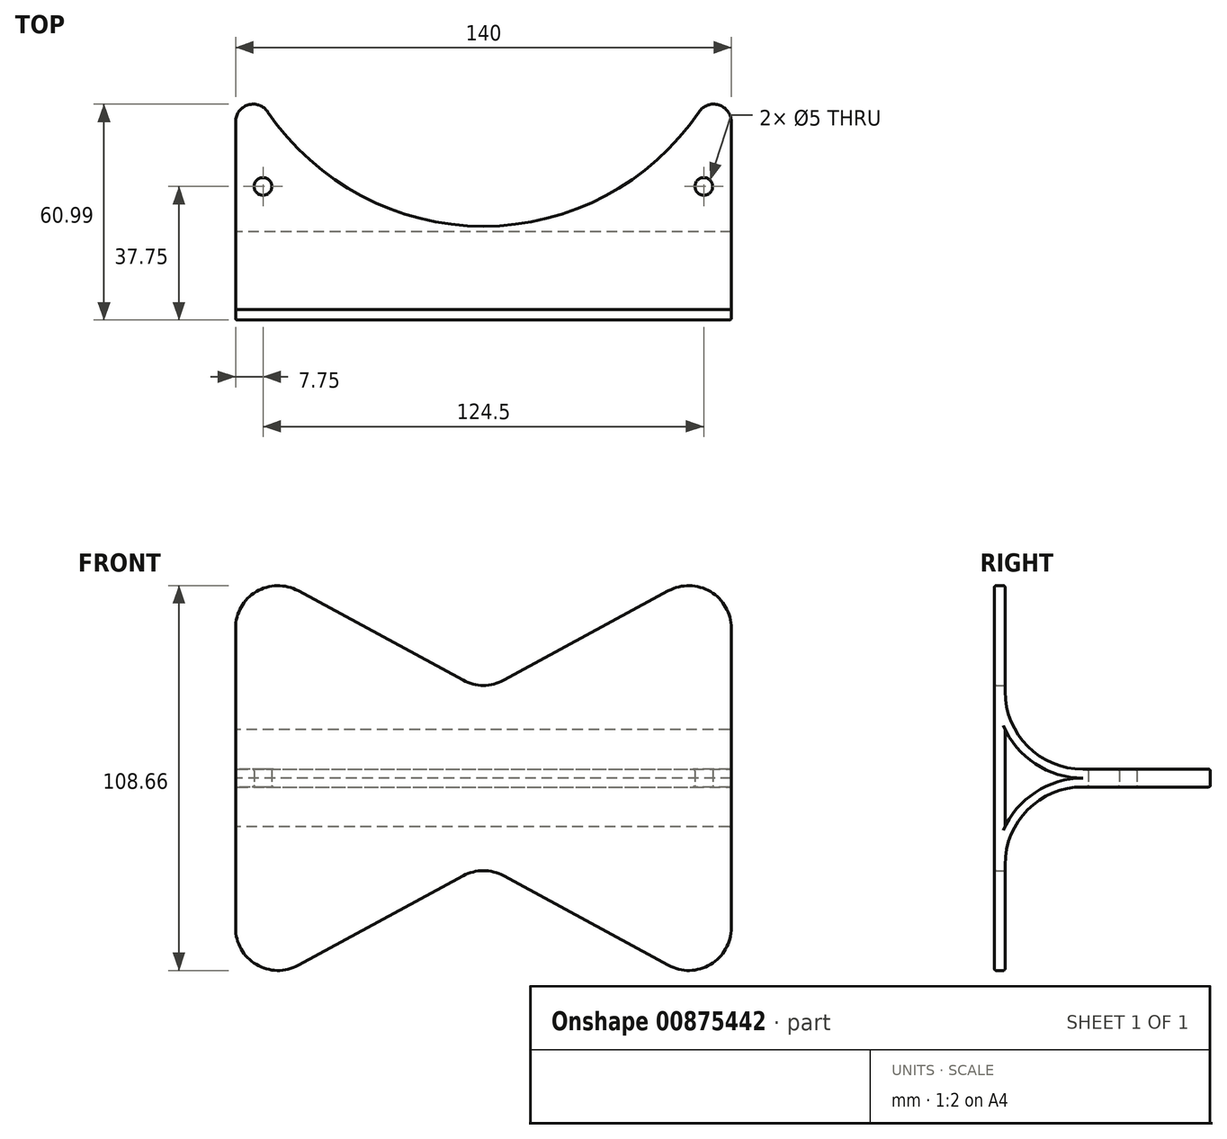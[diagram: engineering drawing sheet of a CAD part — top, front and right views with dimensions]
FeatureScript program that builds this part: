
annotation { "Feature Type Name" : "Feature", "Feature Type Description" : "" }
export const myFeature = defineFeature(function(context is Context, id is Id, definition is map)
    precondition{}
    {
        {
            var Q0;
            Q0=qCreatedBy(makeId("Top.planeOp"),FACE);
            var sketch = newSketch(context, id + "F0", { "sketchPlane" : qUnion([Q0])});
            skArc(sketch, "E0", {"start": v(-70, -22.41) * mm, "mid": v(0, -73.5) * mm, "end": v(70, -22.41) * mm});
            skLineSegment(sketch, "E1", {"start": v(-70, -22.41) * mm, "end": v(-70, -75) * mm});
            skLineSegment(sketch, "E2", {"start": v(-70, -75) * mm, "end": v(70, -75) * mm});
            skLineSegment(sketch, "E3", {"start": v(70, -75) * mm, "end": v(70, -22.41) * mm});
            skCircle(sketch, "E4", {"center": v(62.25, -62.25) * mm, "radius": 2.5 * mm});
            skLineSegment(sketch, "E5", {"start": v(0, 26.99) * mm, "end": v(0, -105.78) * mm, "construction": true});
            skCircle(sketch, "E6.MirrorC", {"center": v(-62.25, -62.25) * mm, "radius": 2.5 * mm});
            skSolve(sketch);
        }
        {
            var Q0;
            Q0=qSketchRegion(id+"F0",true);
            extrude(context, id + "F1", {"entities" : qUnion([Q0]), "depth" : 5 * mm, "offsetDistance" : 25 * mm});
        }
        {
            var Q0;
            Q0=makeQuery(id+"F1.opExtrude","SWEPT_FACE",FACE,{"disambiguationData":[OSD([sQuery(id+"F0.wireOp",EDGE,"E1")])]});
            var sketch = newSketch(context, id + "F2", { "sketchPlane" : qUnion([Q0])});
            skArc(sketch, "E7", {"start": v(97, -22) * mm, "mid": v(90.56, -6.44) * mm, "end": v(75, 0) * mm});
            skArc(sketch, "E8", {"start": v(75, 5) * mm, "mid": v(90.56, 11.44) * mm, "end": v(97, 27) * mm});
            skLineSegment(sketch, "E9.bottom", {"start": v(97, -60) * mm, "end": v(100, -60) * mm});
            skLineSegment(sketch, "E9.top", {"start": v(97, 65) * mm, "end": v(100, 65) * mm});
            skLineSegment(sketch, "E9.left", {"start": v(97, -60) * mm, "end": v(97, -22) * mm});
            skLineSegment(sketch, "E9.right", {"start": v(100, -60) * mm, "end": v(100, 65) * mm});
            skArc(sketch, "E10", {"start": v(97, -11.22) * mm, "mid": v(87.96, -1.21) * mm, "end": v(75, 2.5) * mm});
            skArc(sketch, "E11", {"start": v(75, 2.5) * mm, "mid": v(87.96, 6.21) * mm, "end": v(97, 16.22) * mm});
            skLineSegment(sketch, "E12", {"start": v(75, 0) * mm, "end": v(75, 2.5) * mm});
            skLineSegment(sketch, "E13", {"start": v(75, 2.5) * mm, "end": v(75, 5) * mm});
            skLineSegment(sketch, "E14.trimOffspring", {"start": v(97, -11.22) * mm, "end": v(97, 16.22) * mm});
            skLineSegment(sketch, "E15.trimOffspring", {"start": v(97, 27) * mm, "end": v(97, 65) * mm});
            skSolve(sketch);
        }
        {
            var Q0;
            Q0=qSketchRegion(id+"F2",true);
            var Q1;
            Q1=makeQuery(id+"F1.opExtrude","SWEPT_FACE",FACE,{"disambiguationData":[OSD([sQuery(id+"F0.wireOp",EDGE,"E3")])]});
            extrude(context, id + "F3", {"entities" : qUnion([Q0]), "operationType" : NewBodyOperationType.ADD, "endBound" : BoundingType.UP_TO_SURFACE, "oppositeDirection" : true, "depth" : 25 * mm, "endBoundEntityFace" : qUnion([Q1]), "offsetDistance" : 25 * mm});
        }
        {
            var Q0;
            Q0=makeQuery(id+"F2.imprint","IMPRINT",FACE,{"disambiguationData":[TD([[makeQuery(id+"F2.imprint","IMPRINT",EDGE,{"derivedFrom":sQuery(id+"F2.wireOp",EDGE,"E10")}),-1.0]])]});
            extrude(context, id + "F4", {"entities" : qUnion([Q0]), "operationType" : NewBodyOperationType.REMOVE, "endBound" : BoundingType.THROUGH_ALL, "oppositeDirection" : true, "depth" : 25 * mm, "offsetDistance" : 25 * mm});
        }
        {
            var Q0;
            Q0=makeQuery(id+"F1.opExtrude","SWEPT_EDGE",EDGE,{"disambiguationData":[OSD([sQuery(id+"F0.wireOp",EDGE,"E0"),sQuery(id+"F0.wireOp",EDGE,"E3")])]});
            var Q1;
            Q1=makeQuery(id+"F1.opExtrude","SWEPT_EDGE",EDGE,{"disambiguationData":[OSD([sQuery(id+"F0.wireOp",EDGE,"E0"),sQuery(id+"F0.wireOp",EDGE,"E1")])]});
            fillet(context, id + "F5", {"entities" : qUnion([Q0, Q1]), "radius" : 5 * mm, "tangentPropagation" : true, "allowEdgeOverflow" : false});
        }
        {
            var Q0;
            Q0=makeQuery(id+"F3.opExtrude","SWEPT_FACE",FACE,{"disambiguationData":[OSD([sQuery(id+"F2.wireOp",EDGE,"E15.trimOffspring")])]});
            var sketch = newSketch(context, id + "F6", { "sketchPlane" : qUnion([Q0])});
            skPoint(sketch, "E16.middle", {"position": v(0, 46) * mm});
            skLineSegment(sketch, "E17", {"start": v(-105.3, 2.5) * mm, "end": v(109.3, 2.5) * mm, "construction": true});
            skLineSegment(sketch, "E18", {"start": v(0, 17.77) * mm, "end": v(0, 82.4) * mm, "construction": true});
            skPoint(sketch, "E18.startSnap0", {"position": v(0, 27) * mm});
            skLineSegment(sketch, "E19.MirrorCS", {"start": v(70, 65) * mm, "end": v(0, 27) * mm});
            skLineSegment(sketch, "E20", {"start": v(70, 65) * mm, "end": v(0, 65) * mm});
            skLineSegment(sketch, "E21.MirrorCS", {"start": v(-70, 65) * mm, "end": v(0, 65) * mm});
            skLineSegment(sketch, "E22.MirrorCS", {"start": v(-70, 65) * mm, "end": v(0, 27) * mm});
            skLineSegment(sketch, "E23.MirrorCS", {"start": v(70, -60) * mm, "end": v(0, -22) * mm});
            skLineSegment(sketch, "E24.MirrorCS", {"start": v(-70, -60) * mm, "end": v(0, -22) * mm});
            skLineSegment(sketch, "E25.MirrorCS", {"start": v(-70, -60) * mm, "end": v(0, -60) * mm});
            skLineSegment(sketch, "E26.MirrorCS", {"start": v(70, -60) * mm, "end": v(0, -60) * mm});
            skSolve(sketch);
        }
        {
            var Q0;
            Q0=qSketchRegion(id+"F6",true);
            extrude(context, id + "F7", {"entities" : qUnion([Q0]), "operationType" : NewBodyOperationType.REMOVE, "endBound" : BoundingType.THROUGH_ALL, "oppositeDirection" : true, "depth" : 25 * mm, "offsetDistance" : 25 * mm});
        }
        {
            var Q0;
            Q0=makeQuery(id+"F7.boolean.opBoolean","COPY",EDGE,{"derivedFrom":makeQuery(id+"F7.opExtrude","SWEPT_EDGE",EDGE,{"disambiguationData":[OSD([sQuery(id+"F2.wireOp",EDGE,"E8"),sQuery(id+"F2.wireOp",EDGE,"E15.trimOffspring"),sQuery(id+"F6.wireOp",EDGE,"E19.MirrorCS"),sQuery(id+"F6.wireOp",EDGE,"E22.MirrorCS")])]})});
            var Q1;
            Q1=makeQuery(id+"F7.boolean.opBoolean","MERGE",EDGE,{"derivedFrom":[makeQuery(id+"F3.opExtrude","CAP_EDGE",EDGE,{"disambiguationData":[OSD([sQuery(id+"F2.wireOp",EDGE,"E9.top")])],"isStart":true})],"fromTools":[makeQuery(id+"F7.opExtrude","SWEPT_EDGE",EDGE,{"disambiguationData":[OSD([sQuery(id+"F2.wireOp",EDGE,"E15.trimOffspring"),sQuery(id+"F6.wireOp",EDGE,"E19.MirrorCS"),sQuery(id+"F6.wireOp",EDGE,"E20")])]})]});
            var Q2;
            Q2=makeQuery(id+"F7.boolean.opBoolean","MERGE",EDGE,{"derivedFrom":[makeQuery(id+"F3.opExtrude","CAP_EDGE",EDGE,{"disambiguationData":[OSD([sQuery(id+"F2.wireOp",EDGE,"E9.top")])],"isStart":false})],"fromTools":[makeQuery(id+"F7.opExtrude","SWEPT_EDGE",EDGE,{"disambiguationData":[OSD([sQuery(id+"F2.wireOp",EDGE,"E15.trimOffspring"),sQuery(id+"F6.wireOp",EDGE,"E21.MirrorCS"),sQuery(id+"F6.wireOp",EDGE,"E22.MirrorCS")])]})]});
            var Q3;
            Q3=makeQuery(id+"F7.boolean.opBoolean","COPY",EDGE,{"derivedFrom":makeQuery(id+"F7.opExtrude","SWEPT_EDGE",EDGE,{"disambiguationData":[OSD([sQuery(id+"F6.wireOp",EDGE,"E23.MirrorCS"),sQuery(id+"F6.wireOp",EDGE,"E24.MirrorCS")])]})});
            var Q4;
            Q4=makeQuery(id+"F7.boolean.opBoolean","MERGE",EDGE,{"derivedFrom":[makeQuery(id+"F3.opExtrude","CAP_EDGE",EDGE,{"disambiguationData":[OSD([sQuery(id+"F2.wireOp",EDGE,"E9.bottom")])],"isStart":true})],"fromTools":[makeQuery(id+"F7.opExtrude","SWEPT_EDGE",EDGE,{"disambiguationData":[OSD([sQuery(id+"F6.wireOp",EDGE,"E23.MirrorCS"),sQuery(id+"F6.wireOp",EDGE,"E26.MirrorCS")])]})]});
            var Q5;
            Q5=makeQuery(id+"F7.boolean.opBoolean","MERGE",EDGE,{"derivedFrom":[makeQuery(id+"F3.opExtrude","CAP_EDGE",EDGE,{"disambiguationData":[OSD([sQuery(id+"F2.wireOp",EDGE,"E9.bottom")])],"isStart":false})],"fromTools":[makeQuery(id+"F7.opExtrude","SWEPT_EDGE",EDGE,{"disambiguationData":[OSD([sQuery(id+"F6.wireOp",EDGE,"E24.MirrorCS"),sQuery(id+"F6.wireOp",EDGE,"E25.MirrorCS")])]})]});
            fillet(context, id + "F8", {"entities" : qUnion([Q0, Q1, Q2, Q3, Q4, Q5]), "radius" : 12 * mm, "tangentPropagation" : true, "allowEdgeOverflow" : false});
        }
        {
            var Q0;
            Q0=makeQuery(id+"F1.opExtrude","CAP_EDGE",EDGE,{"disambiguationData":[OSD([sQuery(id+"F0.wireOp",EDGE,"E0")])],"isStart":true});
            var Q1;
            Q1=makeQuery(id+"F3.opExtrude","SWEPT_FACE",FACE,{"disambiguationData":[OSD([sQuery(id+"F2.wireOp",EDGE,"E9.bottom")])]});
            var Q2;
            Q2=makeQuery(id+"F7.boolean.opBoolean","COPY",FACE,{"derivedFrom":makeQuery(id+"F7.opExtrude","SWEPT_FACE",FACE,{"disambiguationData":[OSD([sQuery(id+"F6.wireOp",EDGE,"0e32ecbb-843a-458c-b420-3e7b3406acce4.MirrorCS")])]})});
            var Q3;
            Q3=makeQuery(id+"F7.boolean.opBoolean","COPY",FACE,{"derivedFrom":makeQuery(id+"F7.opExtrude","SWEPT_FACE",FACE,{"disambiguationData":[OSD([sQuery(id+"F6.wireOp",EDGE,"0e32ecbb-843a-458c-b420-3e7b3406acce13.MirrorCS")])]})});
            var Q4;
            Q4=makeQuery(id+"F7.boolean.opBoolean","COPY",FACE,{"derivedFrom":makeQuery(id+"F7.opExtrude","SWEPT_FACE",FACE,{"disambiguationData":[OSD([sQuery(id+"F6.wireOp",EDGE,"0e32ecbb-843a-458c-b420-3e7b3406acce12.MirrorCS")])]})});
            var Q5;
            Q5=makeQuery(id+"F7.boolean.opBoolean","COPY",FACE,{"derivedFrom":makeQuery(id+"F7.opExtrude","SWEPT_FACE",FACE,{"disambiguationData":[OSD([sQuery(id+"F6.wireOp",EDGE,"0e32ecbb-843a-458c-b420-3e7b3406acce3.MirrorCS")])]})});
            var Q6;
            Q6=makeQuery(id+"F4.boolean.opBoolean","COPY",EDGE,{"derivedFrom":makeQuery(id+"F4.opExtrude","CAP_EDGE",EDGE,{"disambiguationData":[OSD([sQuery(id+"F2.wireOp",EDGE,"E14.trimOffspring")])],"isStart":true})});
            var Q7;
            Q7=makeQuery(id+"F3.opExtrude","SWEPT_FACE",FACE,{"disambiguationData":[OSD([sQuery(id+"F2.wireOp",EDGE,"E8")])]});
            var Q8;
            Q8=makeQuery(id+"F7.boolean.opBoolean","COPY",FACE,{"derivedFrom":makeQuery(id+"F7.opExtrude","SWEPT_FACE",FACE,{"disambiguationData":[OSD([sQuery(id+"F6.wireOp",EDGE,"E16.top")])]})});
            var Q9;
            Q9=makeQuery(id+"F7.boolean.opBoolean","COPY",FACE,{"derivedFrom":makeQuery(id+"F7.opExtrude","SWEPT_FACE",FACE,{"disambiguationData":[OSD([sQuery(id+"F6.wireOp",EDGE,"Ly1mIHWL-rzSR-9UTr-SM5t-WTGvqKfeCDd2.left")])]})});
            var Q10;
            Q10=makeQuery(id+"F7.boolean.opBoolean","COPY",FACE,{"derivedFrom":makeQuery(id+"F7.opExtrude","SWEPT_FACE",FACE,{"disambiguationData":[OSD([sQuery(id+"F6.wireOp",EDGE,"ovKNdTth-XfNB-p8zx-q9Qh-aN19TmUE7MYe")])]})});
            var Q11;
            Q11=makeQuery(id+"F7.boolean.opBoolean","COPY",FACE,{"derivedFrom":makeQuery(id+"F7.opExtrude","SWEPT_FACE",FACE,{"disambiguationData":[OSD([sQuery(id+"F6.wireOp",EDGE,"70ea626d-60c3-431f-a16c-7614d6506252.trimOffspring")])]})});
            var Q12;
            Q12=makeQuery(id+"F3.opExtrude","SWEPT_FACE",FACE,{"disambiguationData":[OSD([sQuery(id+"F2.wireOp",EDGE,"E15.trimOffspring")])]});
            var Q13;
            Q13=makeQuery(id+"F4.boolean.opBoolean","INTERSECT",EDGE,{"derivedFrom":[makeQuery(id+"F3.boolean.opBoolean","MERGE",FACE,{"derivedFrom":[makeQuery(id+"F1.opExtrude","SWEPT_FACE",FACE,{"disambiguationData":[OSD([sQuery(id+"F0.wireOp",EDGE,"E3")])]}),makeQuery(id+"F3.opExtrude","CAP_FACE",FACE,{"disambiguationData":[OSD([sQuery(id+"F2.wireOp",EDGE,"E7"),sQuery(id+"F2.wireOp",EDGE,"E8"),sQuery(id+"F2.wireOp",EDGE,"E9.bottom"),sQuery(id+"F2.wireOp",EDGE,"E9.top"),sQuery(id+"F2.wireOp",EDGE,"E9.left"),sQuery(id+"F2.wireOp",EDGE,"E9.right"),sQuery(id+"F2.wireOp",EDGE,"E12"),sQuery(id+"F2.wireOp",EDGE,"E13"),sQuery(id+"F2.wireOp",EDGE,"E15.trimOffspring")])],"isStart":false})]}),makeQuery(id+"F4.opExtrude","SWEPT_FACE",FACE,{"disambiguationData":[OSD([sQuery(id+"F2.wireOp",EDGE,"E14.trimOffspring")])]})]});
            var Q14;
            Q14=makeQuery(id+"F3.opExtrude","CAP_EDGE",EDGE,{"disambiguationData":[OSD([sQuery(id+"F2.wireOp",EDGE,"E9.right")])],"isStart":false});
            var Q15;
            Q15=makeQuery(id+"F3.opExtrude","SWEPT_EDGE",EDGE,{"disambiguationData":[OSD([sQuery(id+"F2.wireOp",EDGE,"E9.top"),sQuery(id+"F2.wireOp",EDGE,"E9.right")])]});
            var Q16;
            Q16=makeQuery(id+"F3.opExtrude","CAP_EDGE",EDGE,{"disambiguationData":[OSD([sQuery(id+"F2.wireOp",EDGE,"E9.right")])],"isStart":true});
            var Q17;
            Q17=makeQuery(id+"F1.opExtrude","SWEPT_FACE",FACE,{"disambiguationData":[OSD([sQuery(id+"F0.wireOp",EDGE,"E4")])]});
            var Q18;
            Q18=makeQuery(id+"F1.opExtrude","SWEPT_FACE",FACE,{"disambiguationData":[OSD([sQuery(id+"F0.wireOp",EDGE,"E6.MirrorC")])]});
            fillet(context, id + "F9", {"entities" : qUnion([Q0, Q1, Q2, Q3, Q4, Q5, Q6, Q7, Q8, Q9, Q10, Q11, Q12, Q13, Q14, Q15, Q16, Q17, Q18]), "radius" : .5 * mm, "tangentPropagation" : true, "allowEdgeOverflow" : false});
        }
    });
